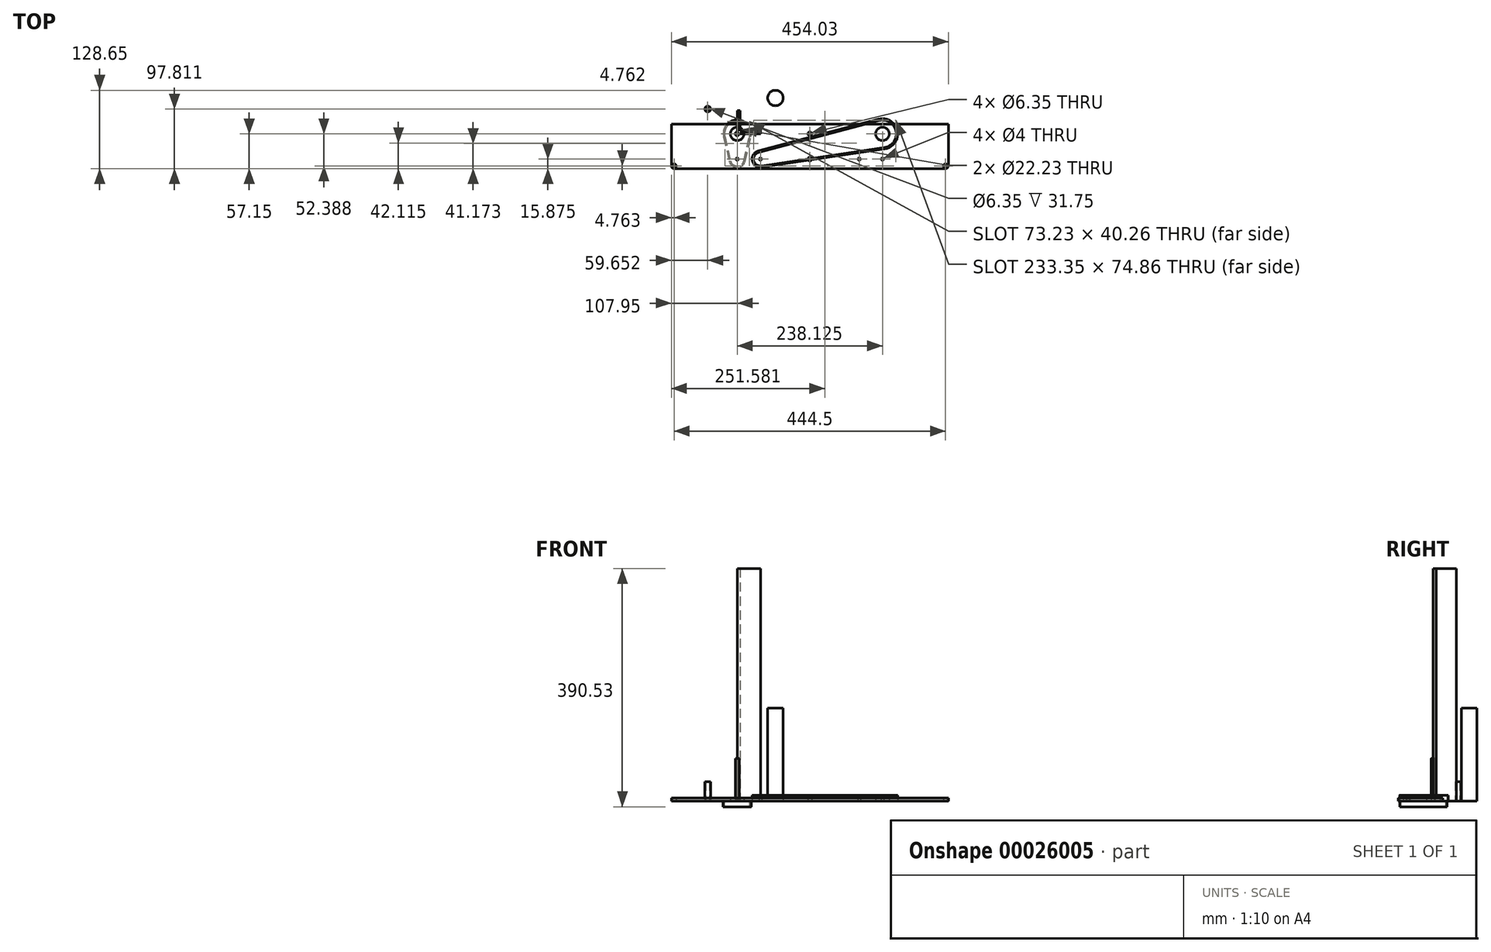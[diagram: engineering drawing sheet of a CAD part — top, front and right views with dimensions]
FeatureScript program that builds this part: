
annotation { "Feature Type Name" : "Feature", "Feature Type Description" : "" }
export const myFeature = defineFeature(function(context is Context, id is Id, definition is map)
    precondition{}
    {
        {
            var Q0;
            Q0=qCreatedBy(makeId("Top.planeOp"),FACE);
            var sketch = newSketch(context, id + "F0", { "sketchPlane" : qUnion([Q0])});
            skCircle(sketch, "E0", {"center": v(0, 0) * mm, "radius": 107.95 * mm, "construction": true});
            skCircle(sketch, "E1", {"center": v(238.13, 0) * mm, "radius": 107.95 * mm, "construction": true});
            skPoint(sketch, "E2.rect.middle", {"position": v(119.06, 0) * mm});
            skLineSegment(sketch, "E3", {"start": v(238.13, 0) * mm, "end": v(0, 0) * mm, "construction": true});
            skCircle(sketch, "E4", {"center": v(0, 0) * mm, "radius": 11.11 * mm});
            skLineSegment(sketch, "E5", {"start": v(119.06, 0) * mm, "end": v(119.06, 15.88) * mm, "construction": true});
            skCircle(sketch, "E6.MirrorC", {"center": v(238.13, 0) * mm, "radius": 11.11 * mm});
            skLineSegment(sketch, "E7.bottom", {"start": v(-107.95, 15.88) * mm, "end": v(346.08, 15.88) * mm});
            skLineSegment(sketch, "E7.top", {"start": v(-107.95, -57.15) * mm, "end": v(346.08, -57.15) * mm});
            skLineSegment(sketch, "E7.left", {"start": v(-107.95, 15.88) * mm, "end": v(-107.95, -57.15) * mm});
            skLineSegment(sketch, "E7.right", {"start": v(346.08, 15.88) * mm, "end": v(346.08, -57.15) * mm});
            skCircle(sketch, "E8", {"center": v(-103.19, -52.39) * mm, "radius": 3.18 * mm});
            skCircle(sketch, "E9", {"center": v(-103.19, -52.39) * mm, "radius": 4.76 * mm, "construction": true});
            skCircle(sketch, "E10.MirrorC", {"center": v(341.31, -52.39) * mm, "radius": 3.18 * mm});
            skCircle(sketch, "E11", {"center": v(119.06, 0) * mm, "radius": 3.18 * mm});
            skLineSegment(sketch, "E12", {"start": v(-107.95, -20.64) * mm, "end": v(346.08, -20.64) * mm, "construction": true});
            skLineSegment(sketch, "E13", {"start": v(0, 15.88) * mm, "end": v(0, -57.15) * mm, "construction": true});
            skLineSegment(sketch, "E14.MirrorCS", {"start": v(238.13, 15.88) * mm, "end": v(238.13, -57.15) * mm, "construction": true});
            skCircle(sketch, "E15", {"center": v(0, -41.28) * mm, "radius": 2 * mm});
            skLineSegment(sketch, "E16", {"start": v(19.05, -57.15) * mm, "end": v(19.05, -20.64) * mm, "construction": true});
            skCircle(sketch, "E17.MirrorC", {"center": v(38.1, -41.28) * mm, "radius": 2 * mm});
            skCircle(sketch, "E18.MirrorC", {"center": v(119.06, -41.27) * mm, "radius": 3.18 * mm});
            skCircle(sketch, "E19.MirrorC", {"center": v(238.13, -41.28) * mm, "radius": 2 * mm});
            skCircle(sketch, "E20.MirrorC", {"center": v(200.03, -41.28) * mm, "radius": 2 * mm});
            skSolve(sketch);
        }
        {
            var Q0;
            Q0=qSketchRegion(id+"F0",true);
            extrude(context, id + "F1", {"entities" : qUnion([Q0]), "depth" : 4.76 * mm});
        }
        {
            var Q0;
            Q0=qCreatedBy(makeId("Top.planeOp"),FACE);
            var sketch = newSketch(context, id + "F2", { "sketchPlane" : qUnion([Q0])});
            skCircle(sketch, "E21", {"center": v(0, 0) * mm, "radius": 3.17 * mm});
            skSolve(sketch);
        }
        {
            var Q0;
            Q0=qSketchRegion(id+"F2",true);
            extrude(context, id + "F3", {"entities" : qUnion([Q0]), "depth" : 69.85 * mm});
        }
        {
            var Q0;
            Q0=qCreatedBy(makeId("Top.planeOp"),FACE);
            var sketch = newSketch(context, id + "F4", { "sketchPlane" : qUnion([Q0])});
            skCircle(sketch, "E22", {"center": v(-48.3, 40.66) * mm, "radius": 4.76 * mm});
            skCircle(sketch, "E23", {"center": v(-48.3, 40.66) * mm, "radius": 3.18 * mm});
            skSolve(sketch);
        }
        {
            var Q0;
            Q0=qSketchRegion(id+"F4",true);
            extrude(context, id + "F5", {"entities" : qUnion([Q0]), "depth" : 31.75 * mm});
        }
        {
            var Q0;
            Q0=makeQuery(id+"F1.opExtrude","SWEPT_EDGE",EDGE,{"disambiguationData":[OSD([sQuery(id+"F0.wireOp",EDGE,"E7.top"),sQuery(id+"F0.wireOp",EDGE,"E7.left")])]});
            var Q1;
            Q1=makeQuery(id+"F1.opExtrude","SWEPT_EDGE",EDGE,{"disambiguationData":[OSD([sQuery(id+"F0.wireOp",EDGE,"E7.top"),sQuery(id+"F0.wireOp",EDGE,"E7.right")])]});
            fillet(context, id + "F6", {"entities" : qUnion([Q0, Q1]), "radius" : 4.76 * mm, "tangentPropagation" : true, "allowEdgeOverflow" : false});
        }
        {
            var Q0;
            Q0=qCreatedBy(makeId("Top.planeOp"),FACE);
            var sketch = newSketch(context, id + "F7", { "sketchPlane" : qUnion([Q0])});
            skArc(sketch, "E24", {"start": v(35.2, -30.34) * mm, "mid": v(27.02, -43.56) * mm, "end": v(39.77, -52.47) * mm});
            skArc(sketch, "E25", {"start": v(241.46, -22.4) * mm, "mid": v(260.3, 4.58) * mm, "end": v(232.33, 21.89) * mm});
            skLineSegment(sketch, "E26", {"start": v(39.77, -52.47) * mm, "end": v(241.46, -22.4) * mm});
            skLineSegment(sketch, "E27", {"start": v(232.33, 21.89) * mm, "end": v(35.2, -30.34) * mm});
            skArc(sketch, "E28.0", {"start": v(34.62, -28.13) * mm, "mid": v(24.78, -44.02) * mm, "end": v(40.1, -54.73) * mm});
            skLineSegment(sketch, "E28.1", {"start": v(231.74, 24.1) * mm, "end": v(34.62, -28.13) * mm});
            skArc(sketch, "E28.2", {"start": v(241.8, -24.66) * mm, "mid": v(262.54, 5.04) * mm, "end": v(231.74, 24.1) * mm});
            skLineSegment(sketch, "E28.3", {"start": v(40.1, -54.73) * mm, "end": v(241.8, -24.66) * mm});
            skLineSegment(sketch, "E29.0", {"start": v(341.31, -63.5) * mm, "end": v(-103.19, -63.5) * mm});
            skArc(sketch, "E29.1", {"start": v(352.43, -52.39) * mm, "mid": v(349.17, -60.25) * mm, "end": v(341.31, -63.5) * mm});
            skLineSegment(sketch, "E29.2", {"start": v(352.43, 22.23) * mm, "end": v(352.43, -52.39) * mm});
            skLineSegment(sketch, "E29.3", {"start": v(-114.3, 22.23) * mm, "end": v(352.43, 22.23) * mm});
            skLineSegment(sketch, "E29.4", {"start": v(-114.3, -52.39) * mm, "end": v(-114.3, 22.23) * mm});
            skArc(sketch, "E29.5", {"start": v(-103.19, -63.5) * mm, "mid": v(-111.05, -60.25) * mm, "end": v(-114.3, -52.39) * mm});
            skSolve(sketch);
        }
        {
            var Q0;
            Q0=makeQuery(id+"F7.imprint","IMPRINT",FACE,{"disambiguationData":[TD([[makeQuery(id+"F7.imprint","IMPRINT",EDGE,{"derivedFrom":sQuery(id+"F7.wireOp",EDGE,"E24")}),-1.0]])]});
            var Q1;
            {var subQ0=sQuery(id+"F7.wireOp",EDGE,"E29.3");var subQ1=sQuery(id+"F7.wireOp",EDGE,"E25");var subQ2=makeQuery(id+"F7.imprint","INTERSECT",VERTEX,{"disambiguationData":[OD(0.0)],"derivedFrom":[subQ1,subQ0]});Q1=makeQuery(id+"F7.imprint","IMPRINT",FACE,{"disambiguationData":[TD([[makeQuery(id+"F7.imprint","IMPRINT",EDGE,{"disambiguationData":[TD([[subQ2,-1.0]])],"derivedFrom":subQ1}),-1.0]])]});}
            var Q2;
            Q2=sQuery(id+"F7.wireOp",EDGE,"E28.0");
            var Q3;
            Q3=sQuery(id+"F7.wireOp",EDGE,"E24");
            var Q4;
            Q4=sQuery(id+"F7.wireOp",EDGE,"E25");
            var Q5;
            Q5=sQuery(id+"F7.wireOp",EDGE,"E26");
            var Q6;
            Q6=sQuery(id+"F7.wireOp",EDGE,"E27");
            var Q7;
            Q7=sQuery(id+"F7.wireOp",EDGE,"E28.1");
            var Q8;
            Q8=sQuery(id+"F7.wireOp",EDGE,"E28.2");
            var Q9;
            Q9=sQuery(id+"F7.wireOp",EDGE,"E28.3");
            extrude(context, id + "F8", {"entities" : qUnion([Q0, Q1]), "surfaceEntities" : qUnion([Q2, Q3, Q4, Q5, Q6, Q7, Q8, Q9]), "depth" : 9.52 * mm});
        }
        {
            var Q0;
            Q0=qCreatedBy(makeId("Top.planeOp"),FACE);
            var sketch = newSketch(context, id + "F9", { "sketchPlane" : qUnion([Q0])});
            skArc(sketch, "E30", {"start": v(20.1, -4.66) * mm, "mid": v(0, 20.64) * mm, "end": v(-20.1, -4.66) * mm});
            skArc(sketch, "E31", {"start": v(-11.02, -43.83) * mm, "mid": v(0, -52.6) * mm, "end": v(11.02, -43.83) * mm});
            skLineSegment(sketch, "E32", {"start": v(-20.1, -4.66) * mm, "end": v(-11.02, -43.83) * mm});
            skLineSegment(sketch, "E33", {"start": v(11.02, -43.83) * mm, "end": v(20.1, -4.66) * mm});
            skPoint(sketch, "E34.orphan", {"position": v(21.18, 0) * mm});
            skArc(sketch, "E35.0", {"start": v(-13.25, -44.35) * mm, "mid": v(0, -54.88) * mm, "end": v(13.25, -44.35) * mm});
            skLineSegment(sketch, "E35.1", {"start": v(-22.33, -5.18) * mm, "end": v(-13.25, -44.35) * mm});
            skArc(sketch, "E35.2", {"start": v(22.33, -5.18) * mm, "mid": v(0, 22.92) * mm, "end": v(-22.33, -5.18) * mm});
            skLineSegment(sketch, "E35.3", {"start": v(13.25, -44.35) * mm, "end": v(22.33, -5.18) * mm});
            skSolve(sketch);
        }
        {
            var Q0;
            Q0=qSketchRegion(id+"F9",true);
            extrude(context, id + "F10", {"entities" : qUnion([Q0]), "oppositeDirection" : true, "depth" : 9.52 * mm});
        }
        {
            var Q0;
            Q0=qCreatedBy(makeId("Top.planeOp"),FACE);
            var sketch = newSketch(context, id + "F11", { "sketchPlane" : qUnion([Q0])});
            skLineSegment(sketch, "E36", {"start": v(0, 0) * mm, "end": v(0, 38.1) * mm});
            skLineSegment(sketch, "E37", {"start": v(0, 0) * mm, "end": v(38.1, 0) * mm});
            skLineSegment(sketch, "E38.0", {"start": v(4.76, 4.76) * mm, "end": v(4.76, 38.1) * mm});
            skLineSegment(sketch, "E38.1", {"start": v(4.76, 4.76) * mm, "end": v(38.1, 4.76) * mm});
            skLineSegment(sketch, "E39", {"start": v(0, 38.1) * mm, "end": v(4.76, 38.1) * mm});
            skLineSegment(sketch, "E40", {"start": v(38.1, 4.76) * mm, "end": v(38.1, 0) * mm});
            skSolve(sketch);
        }
        {
            var Q0;
            Q0=qSketchRegion(id+"F11",true);
            extrude(context, id + "F12", {"entities" : qUnion([Q0]), "depth" : 381 * mm});
        }
        {
            var Q0;
            Q0=qCreatedBy(makeId("Top.planeOp"),FACE);
            var sketch = newSketch(context, id + "F13", { "sketchPlane" : qUnion([Q0])});
            skCircle(sketch, "E41", {"center": v(62.62, 58.8) * mm, "radius": 12.7 * mm});
            skSolve(sketch);
        }
        {
            var Q0;
            Q0=qSketchRegion(id+"F13",true);
            extrude(context, id + "F14", {"entities" : qUnion([Q0]), "depth" : 152.4 * mm});
        }
        {
            var Q0;
            Q0=makeQuery(id+"F3.opExtrude","CAP_FACE",FACE,{"disambiguationData":[OSD([sQuery(id+"F2.wireOp",EDGE,"E21")])],"isStart":false});
            var sketch = newSketch(context, id + "F15", { "sketchPlane" : qUnion([Q0])});
            skLineSegment(sketch, "E42.left", {"start": v(-0.8, 3.97) * mm, "end": v(-0.8, 2.38) * mm});
            skLineSegment(sketch, "E42.top", {"start": v(-0.8, 2.38) * mm, "end": v(0.8, 2.38) * mm});
            skLineSegment(sketch, "E43", {"start": v(-0.8, 3.17) * mm, "end": v(0.8, 3.17) * mm, "construction": true});
            skLineSegment(sketch, "E42.right", {"start": v(0.8, 3.97) * mm, "end": v(0.8, 2.38) * mm});
            skLineSegment(sketch, "E42.bottom", {"start": v(-0.8, 3.97) * mm, "end": v(0.8, 3.97) * mm});
            skLineSegment(sketch, "E44", {"start": v(0, 3.97) * mm, "end": v(0, 2.38) * mm, "construction": true});
            skSolve(sketch);
        }
        {
            var Q0;
            Q0=qSketchRegion(id+"F15",true);
            extrude(context, id + "F16", {"entities" : qUnion([Q0]), "operationType" : NewBodyOperationType.REMOVE, "endBound" : BoundingType.THROUGH_ALL, "oppositeDirection" : true, "depth" : 25.4 * mm});
        }
    });
